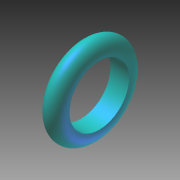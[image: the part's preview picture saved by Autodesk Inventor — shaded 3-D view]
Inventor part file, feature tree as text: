
AUTODESK INVENTOR PART (.ipt)
format: ipt  version: 2012 (Build 160160000, 160)  size: 159,232 bytes
history: native  units: in
note: dims shown in document units (in); Inventor stores cm internally (conversion verified against a paired STEP export)
features: revolve x1, sketch x1
ambient origin geometry x8: Origin, YZ Plane, XZ Plane, XY Plane, X Axis, Y Axis, Z Axis, Center Point
bodies: Solid1 (feature_tree)
feature tree (2):
  revolve  "Revolution1"  [1 undecoded]
  sketch  "Sketch1"  dims[d0=0.0625in d1=0.625in d2=1.0in d3=0.4375in d4=0.3125in d5=0.625in d6=90.0deg]
note: 1 required parameter value undecoded (feature->parameter linkage not recoverable at this tier; creation-order binding heuristic only, values carry confidence <= 0.55)
